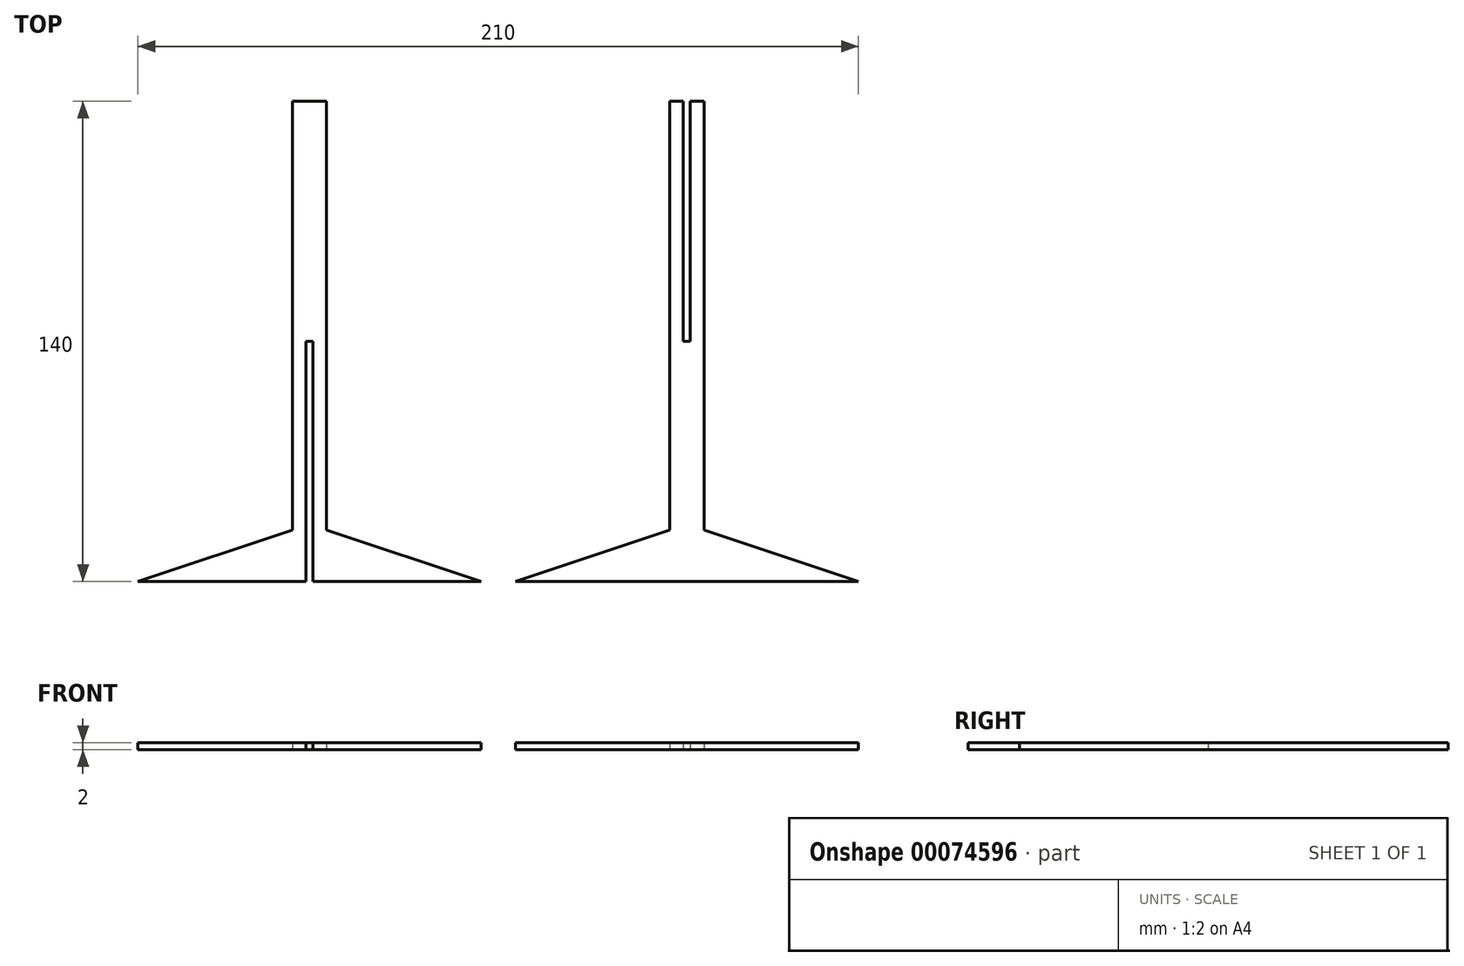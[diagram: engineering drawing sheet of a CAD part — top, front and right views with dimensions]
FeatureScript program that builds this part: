
annotation { "Feature Type Name" : "Feature", "Feature Type Description" : "" }
export const myFeature = defineFeature(function(context is Context, id is Id, definition is map)
    precondition{}
    {
        {
            var Q0;
            Q0=qCreatedBy(makeId("Top.planeOp"),FACE);
            var sketch = newSketch(context, id + "F0", { "sketchPlane" : qUnion([Q0])});
            skLineSegment(sketch, "E0", {"start": v(5, 0) * mm, "end": v(105, 0) * mm});
            skLineSegment(sketch, "E1", {"start": v(105, 0) * mm, "end": v(60, 15) * mm});
            skLineSegment(sketch, "E2", {"start": v(60, 15) * mm, "end": v(60, 140) * mm});
            skLineSegment(sketch, "E3", {"start": v(60, 140) * mm, "end": v(56, 140) * mm});
            skLineSegment(sketch, "E4", {"start": v(56, 140) * mm, "end": v(56, 70) * mm});
            skLineSegment(sketch, "E5", {"start": v(56, 70) * mm, "end": v(54, 70) * mm});
            skLineSegment(sketch, "E6", {"start": v(54, 70) * mm, "end": v(54, 140) * mm});
            skLineSegment(sketch, "E7", {"start": v(54, 140) * mm, "end": v(50, 140) * mm});
            skLineSegment(sketch, "E8", {"start": v(50, 140) * mm, "end": v(50, 15) * mm});
            skLineSegment(sketch, "E9", {"start": v(50, 15) * mm, "end": v(5, 0) * mm});
            skLineSegment(sketch, "E10", {"start": v(-5, 0) * mm, "end": v(-54, 0) * mm});
            skLineSegment(sketch, "E11", {"start": v(-54, 0) * mm, "end": v(-54, 70) * mm});
            skLineSegment(sketch, "E12", {"start": v(-54, 70) * mm, "end": v(-56, 70) * mm});
            skLineSegment(sketch, "E13", {"start": v(-56, 70) * mm, "end": v(-56, 0) * mm});
            skLineSegment(sketch, "E14", {"start": v(-56, 0) * mm, "end": v(-105, 0) * mm});
            skLineSegment(sketch, "E15", {"start": v(-105, 0) * mm, "end": v(-60, 15) * mm});
            skLineSegment(sketch, "E16", {"start": v(-60, 15) * mm, "end": v(-60, 140) * mm});
            skLineSegment(sketch, "E17", {"start": v(-60, 140) * mm, "end": v(-50, 140) * mm});
            skLineSegment(sketch, "E18", {"start": v(-50, 140) * mm, "end": v(-50, 15) * mm});
            skLineSegment(sketch, "E19", {"start": v(-50, 15) * mm, "end": v(-5, 0) * mm});
            skSolve(sketch);
        }
        {
            var Q0;
            Q0=makeQuery(id+"F0.imprint","IMPRINT",FACE,{"disambiguationData":[TD([[makeQuery(id+"F0.imprint","IMPRINT",EDGE,{"derivedFrom":sQuery(id+"F0.wireOp",EDGE,"E10")}),-1.0]])]});
            var Q1;
            Q1=makeQuery(id+"F0.imprint","IMPRINT",FACE,{"disambiguationData":[TD([[makeQuery(id+"F0.imprint","IMPRINT",EDGE,{"derivedFrom":sQuery(id+"F0.wireOp",EDGE,"E0")}),1.0]])]});
            extrude(context, id + "F1", {"entities" : qUnion([Q0, Q1]), "depth" : 2 * mm});
        }
    });
